# Revit family: Haworth_Resonate_ModularLounge
name_source: partatom
category: Furniture
revit_build: Autodesk Revit 2018 (Build: 20170223_1515(x64)
units: mm (PartAtom-declared; Revit-internal decimal feet)

## family parameters
Always vertical = Yes
Cut with Voids When Loaded = No
OmniClass Number = 23.40.70.14.64.11
OmniClass Title = Office Furniture
Room Calculation Point = No
Shared = No
Work Plane-Based = No

## types (3) — shared parameters
Actual Depth = 27.5 "
Actual Height = 33.25 "
Actual Width = 27.5 "
Assembly Code = E2020200
Description = Haworth - Resonate - Modular Lounge
Glide Finish = Haworth _ Polymer _ Slate
Manufacturer = Haworth
Model = SRxx
Note = Veriy Final Dim. w/ Haworth
Revision Number = 1
Seat Height = 17 "
Sustainability Info = http://media.haworth.com
URL = http://www.haworth.com
URL - Product = http://www.haworth.com
Warranty = http://www.haworth.com

## per-type parameters (varying)
| type | Back Support Control | Corner Lounge | Middle Lounge | Ottoman | Side Support Control |
| Straight Back - No Arms | Yes | No | Yes | No | Yes |
| Corner Unit | Yes | Yes | No | No | No |
| Ottoman | No | No | No | Yes | Yes |

## geometry (parser evidence)
native form markers: Blend x9, Sweep x10
no freeform markers — native parametric forms only
